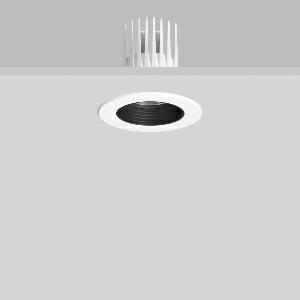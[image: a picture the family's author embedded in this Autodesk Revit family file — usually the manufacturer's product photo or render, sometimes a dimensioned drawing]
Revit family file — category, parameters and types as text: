
# Revit family: heledon_mini_e_901752_002_1_8ab1
name_source: partatom
category: Lighting Fixtures
units: mm (PartAtom-declared; Revit-internal decimal feet)

## family parameters
Cut with Voids When Loaded = No
Host = Face
Light Source = No
Part Type = Normal
Room Calculation Point = No
Round Connector Dimension = Use Diameter
Shared = No

## types (1)
- HELEDON mini E (1 x LED Modul 940, 3200 lm, 4000)
    Apparent Load = 29 VA
    Approval mark = CE
    CIE Flux Codes = 96 100 100 100 100
    Color Rendering = 92
    Color Temperature = 4000
    Default Elevation = 1800 mm
    Description = Series: HELEDON mini
Round recessed downlight. Housing: die-cast aluminium, powder-coated. Black plastic ring and recessed LED to prevent glare from the side. Optical assembly with lens made of plastic (polycarbonate) for the best homogeneous light distribution - can be changed without tools. Best colour rendering index Ra>90. Suitable for Recessed ceiling mounting. Installation without tools thanks to spring fastening system. Including separate LED converter with connecting cable 600 mm.High quality converter without flickering and stroboscopic effect. Through-wiring box (5 pole) available as accessory. The following accessories can be mounted without use of tools: interchangeable lenses, decorative glasses, honeycomb louvre, clear and frosted diffusers, white interchangeable plastic ring. 
Colour: traffic white, matt (RAL 9016)
Diameter: 124 mm
Height: 3 mm
Cut-out diameter: 114 mm
Recess height: 170 mm
Luminaire: recess height: 120 mm
Lamp: LED
Socket: without socket
Colour temperature: 4000K
Colour rendering index (CRI): 92
System power: 29 W
Rated luminous flux: 3200 lm
Luminous efficiency: 110 lm/W
Control gear: Regulated power supply
Protection class: II
Type of protection: IP 20
    Height = 0 mm  [stored 0 ft]
    Lamp = 1 x LED Modul 940
    Lamp Light Flux = 3200 lm
    Lamp count = 1
    Length = 124 mm  [stored 0.406824 ft]
    Lifetime = 50000 h
    Luminous efficacy = 110 lm/W
    Manufacturer = RZB
    ModVariant = No
    Model = 901752.002.1
    Mounting Place = Ceiling
    Mounting Type = Recessed
    Number of Poles = 1
    OnlyDefault = Yes
    Power Factor = 1
    Product Name = HELEDON mini E
    Product group = Recessed downlights
    ProductGroupID = 402
    Protection Class = Protection class II
    Protection Degree = IP 20
    RLX_Detail_Level = 1
    RLX_Emergency_Light_Flux = 0 lm
    RLX_Emergency_Type = 0
    RLX_Emergency_Type_DB = No
    RlxData = <blob elided: 126209 chars, md5=d2e5558a>
    Socket = socket
    Standby Power = 0 W
    System Light Flux = 3200 lm
    System Power = 29 W
    Type Comments = Product without accessories
    Type Image = 901656.002.jpg
    URL = http://relux.com
    VarID = ---
    Voltage = 230 V
    Voltage Range = 220-240 V
    Weight = 0.00 kg
    Width = 0 mm  [stored 0 ft]

note: [stored X ft] marks values corroborated as IEEE doubles in the binary element streams (Revit-internal decimal feet)

## geometry (parser evidence)
native form markers: Blend x4, Sweep x11
no freeform markers — native parametric forms only
